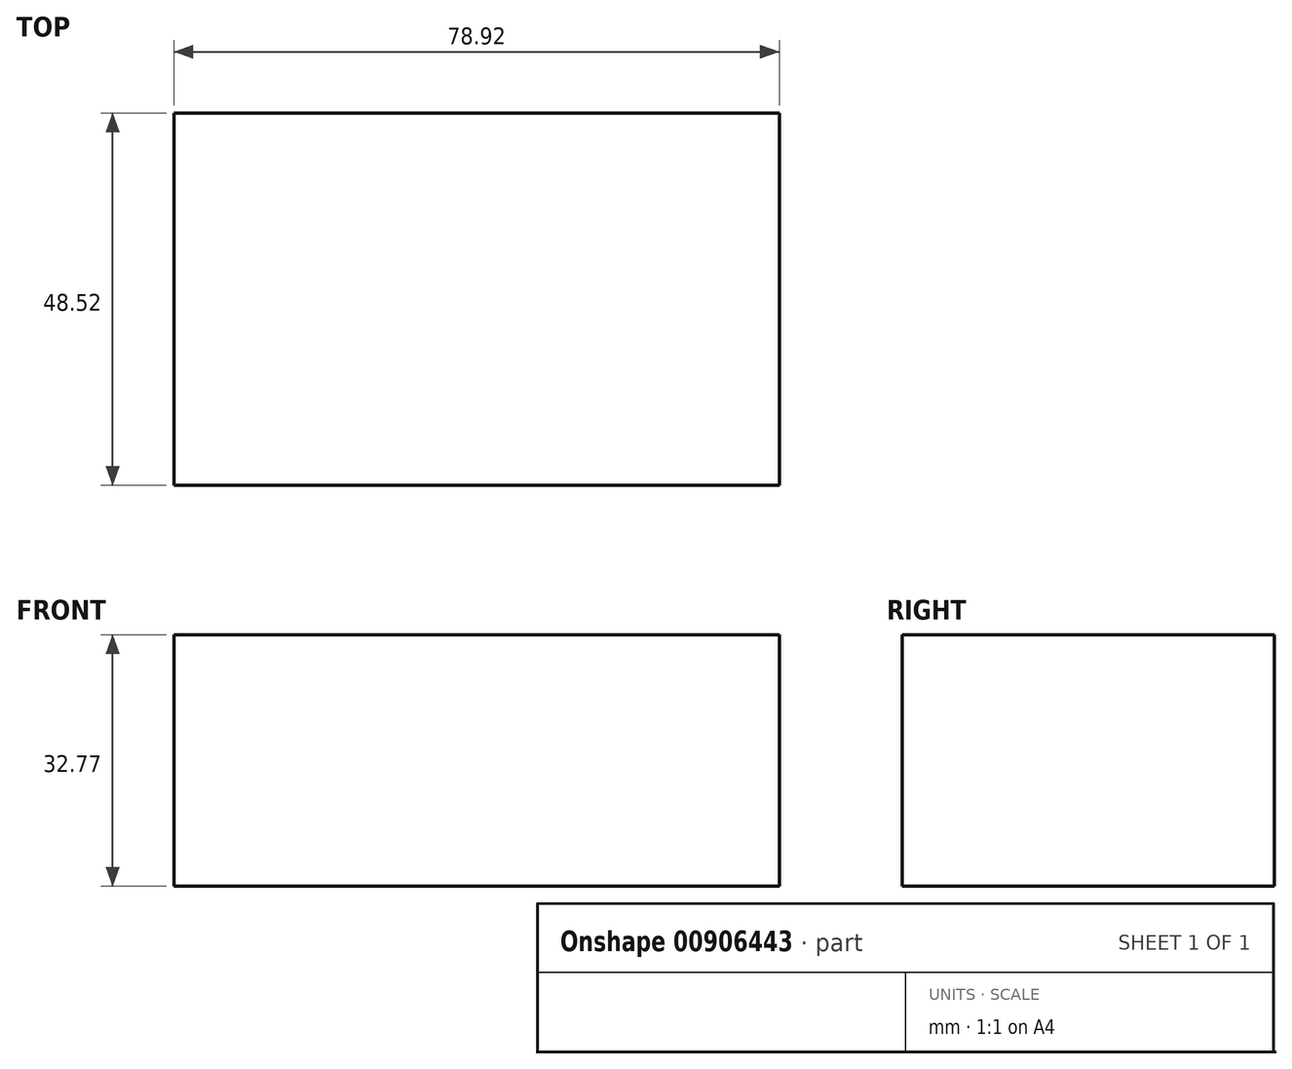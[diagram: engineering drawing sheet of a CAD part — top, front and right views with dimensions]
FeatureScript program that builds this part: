
annotation { "Feature Type Name" : "Feature", "Feature Type Description" : "" }
export const myFeature = defineFeature(function(context is Context, id is Id, definition is map)
    precondition{}
    {
        {
            var Q0;
            Q0=qCreatedBy(makeId("Top.planeOp"),FACE);
            var sketch = newSketch(context, id + "F0", { "sketchPlane" : qUnion([Q0])});
            skLineSegment(sketch, "E0.bottom", {"start": v(-67.97, 26.16) * mm, "end": v(10.95, 26.16) * mm});
            skLineSegment(sketch, "E0.top", {"start": v(-67.97, -22.36) * mm, "end": v(10.95, -22.36) * mm});
            skLineSegment(sketch, "E0.left", {"start": v(-67.97, 26.16) * mm, "end": v(-67.97, -22.36) * mm});
            skLineSegment(sketch, "E0.right", {"start": v(10.95, 26.16) * mm, "end": v(10.95, -22.36) * mm});
            skSolve(sketch);
        }
        {
            var Q0;
            Q0=makeQuery(id+"F0.imprint","IMPRINT",FACE,{"disambiguationData":[TD([[makeQuery(id+"F0.imprint","IMPRINT",EDGE,{"derivedFrom":sQuery(id+"F0.wireOp",EDGE,"E0.bottom")}),-1.0]])]});
            extrude(context, id + "F1", {"entities" : qUnion([Q0]), "depth" : 32.77 * mm, "offsetDistance" : 25.4 * mm});
        }
    });
